# Revit family: 210_d3ecc1fba41d4ef7a4ff1c033c12a4
name_source: partatom
category: Mechanical Equipment
units: mm (PartAtom-declared; Revit-internal decimal feet)

## family parameters
Always vertical = Yes
Cut with Voids When Loaded = No
Part Type = Breaks Into
Room Calculation Point = No
Round Connector Dimension = Use Diameter
Shared = No
Work Plane-Based = No

## types (2) — shared parameters
A2 = 155 mm  [stored 0.50853 ft]
BB = 79 mm  [stored 0.259186 ft]
BB_2 = 40 mm  [stored 0.131234 ft]
BB__ve = -79 mm  [stored -0.259186 ft]
CAT0 = Yes
D = 125 mm
Description = Roof fan
H4 = 99 mm  [stored 0.324803 ft]
H5 = 20 mm  [stored 0.0656168 ft]
H6 = 30 mm  [stored 0.0984252 ft]
H7 = 246 mm
HS = 8 mm  [stored 0.0262467 ft]
Manufacturer = Vilpe
N110 = Yes
P110 = No
QmdConnectorList = 201;D
R = 63 mm
R2 = 112 mm  [stored 0.367454 ft]
R3 = 132 mm
R31 = 143 mm
R32 = 149 mm
R4 = 151 mm  [stored 0.495407 ft]
R5 = 147 mm
R6 = 140 mm
R7 = 88 mm  [stored 0.288714 ft]
RS = 20 mm  [stored 0.0656168 ft]
URL = vilpe.com
W = 500 mm
XS = 186 mm  [stored 0.610236 ft]
Z2 = 70 mm  [stored 0.229659 ft]
Z3 = 40 mm  [stored 0.131234 ft]
Z4 = 59 mm  [stored 0.19357 ft]
magiPartTypeId = 210
magiProductFamilyId = d3ecc1fba41d4ef7a4ff1c033c12a4
zero-valued in all types: Default Elevation

## per-type parameters (varying)
| type | H2 | H8 | HP | magiProductId |
| ECo Flow 125P 500 | 343 mm  [stored 1.12533 ft] | 75 mm  [stored 0.246063 ft] | 99 mm  [stored 0.324803 ft] | b66f9c4426424ed0a39bade3cc1c1e |
| ECo Flow 125P 700 | 541 mm  [stored 1.77493 ft] | 195 mm  [stored 0.639764 ft] | 177 mm  [stored 0.580709 ft] | ebe409c4d98643059e3820509245e5 |

note: column(s) folded — value = type name in every type: MC Product Code

note: [stored X ft] marks values corroborated as IEEE doubles in the binary element streams (Revit-internal decimal feet)

## geometry (parser evidence)
native form markers: Sweep x1
no freeform markers — native parametric forms only
